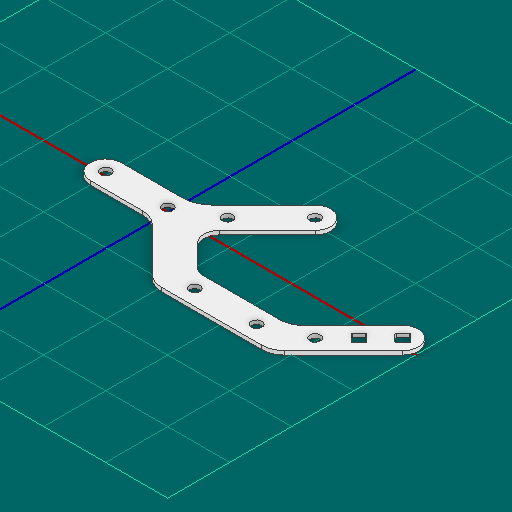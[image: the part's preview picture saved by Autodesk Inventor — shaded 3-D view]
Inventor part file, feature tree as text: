
AUTODESK INVENTOR PART (.ipt)
format: ipt  version: 2025 (Build 290162000, 162)  size: 179,712 bytes
history: native  units: in
note: dims shown in document units (in); Inventor stores cm internally (conversion verified against a paired STEP export)
features: other x3, extrude x1, sketch x1
ambient origin geometry x8: Origin, YZ Plane, XZ Plane, XY Plane, X Axis, Y Axis, Z Axis, Center Point
bodies: Solid1 (feature_tree)
feature tree (5):
  other  "Blocks"
  extrude  "Extrusion1"  TaperAngle=135.0deg  [1 undecoded]
  sketch  "Sketch1"  dims[d5=0.5in d6=135.0deg d7=0.375in d8=0.5in d9=0.375in d10=0.375in d11=0.5in d12=0.1875in d13=0.0625in d14=0.0in d15=1.25in d16=0.5in d17=45.0deg d18=0.25in d19=0.172in d20=0.25in d24=0.172in]
  other  "main"
  other  "main:1"
note: 1 required parameter value undecoded (feature->parameter linkage not recoverable at this tier; creation-order binding heuristic only, values carry confidence <= 0.55)
